# Revit family: Furniture_Other_Sjobergs_Ironing_Table
name_source: partatom
category: Furniture
revit_build: Autodesk Revit 2017 (Build: 20190508_0315(x64)
units: mm (PartAtom-declared; Revit-internal decimal feet)

## family parameters
Always vertical = Yes
Cut with Voids When Loaded = No
OmniClass Number = 23.40.20.27.21
OmniClass Title = Mobile Storage Units
Room Calculation Point = No
Shared = No
Work Plane-Based = No

## types (1)
- Ironing Table
    AssetType = Movable
    BIMObjectName = Furniture_Other_Sjobergs_Ironing_Table
    Brand = Sjöbergs
    Category = School, textile craft
    Color = Wooden
    ConvergoRefNr = 0184-2005-00010-SE
    Cost = 0 $
    Features = One or two ironing boards can be installed diagonally on the same table.
    IfcExportAs = IfcFurnishingElementType
    IfcExportType = TABLE
    IroningTableMainMaterial = Beech
    IroningTableSecondaryMaterial = Table texture
    MainColor = Wooden
    ManufacterURL = https://www.sjobergs.se
    Manufacturer = Sjöbergs
    ManufacturerName = Sjöbergs
    Material = Wood & Metal
    Model = Ironing Table
    ModelNumber = 33062
    NBSDescription = School art, design and technology tables and workbenches;
    NBSReference = 45-35-20/320
    Name = Sjobergs_Ironing_Table
    NominalDepth = 910 mm
    NominalHeight = 897 mm  [stored 2.94291 ft]
    NominalWidth = 1958 mm
    ProductDatasheet = https://www.sjobergs.se
    ProductInformation = A complete ironing table consisting of board 33107 covered with heat-resistant silicone fabric. Stand 33111 in beech. Ironing board 33116 extendable, covered with heat-resistant silicone fabric. Grid 33119 for hot iron in chromed steel.
    Shape = Rectangular
    Size = 1950x910x900 mm
    URL = https://www.sjobergs.se
    Uniclass2 = Pr_40_70_46_42
    Uniclass2015Description = Ironing tables
    Uniclass2015Reference = Pr_40_70_46_42
    Version = 1
    VersionDate = 30/06/2020
    Weight = 70 kg

note: [stored X ft] marks values corroborated as IEEE doubles in the binary element streams (Revit-internal decimal feet)

## geometry (parser evidence)
native form markers: Sweep x5
no freeform markers — native parametric forms only
